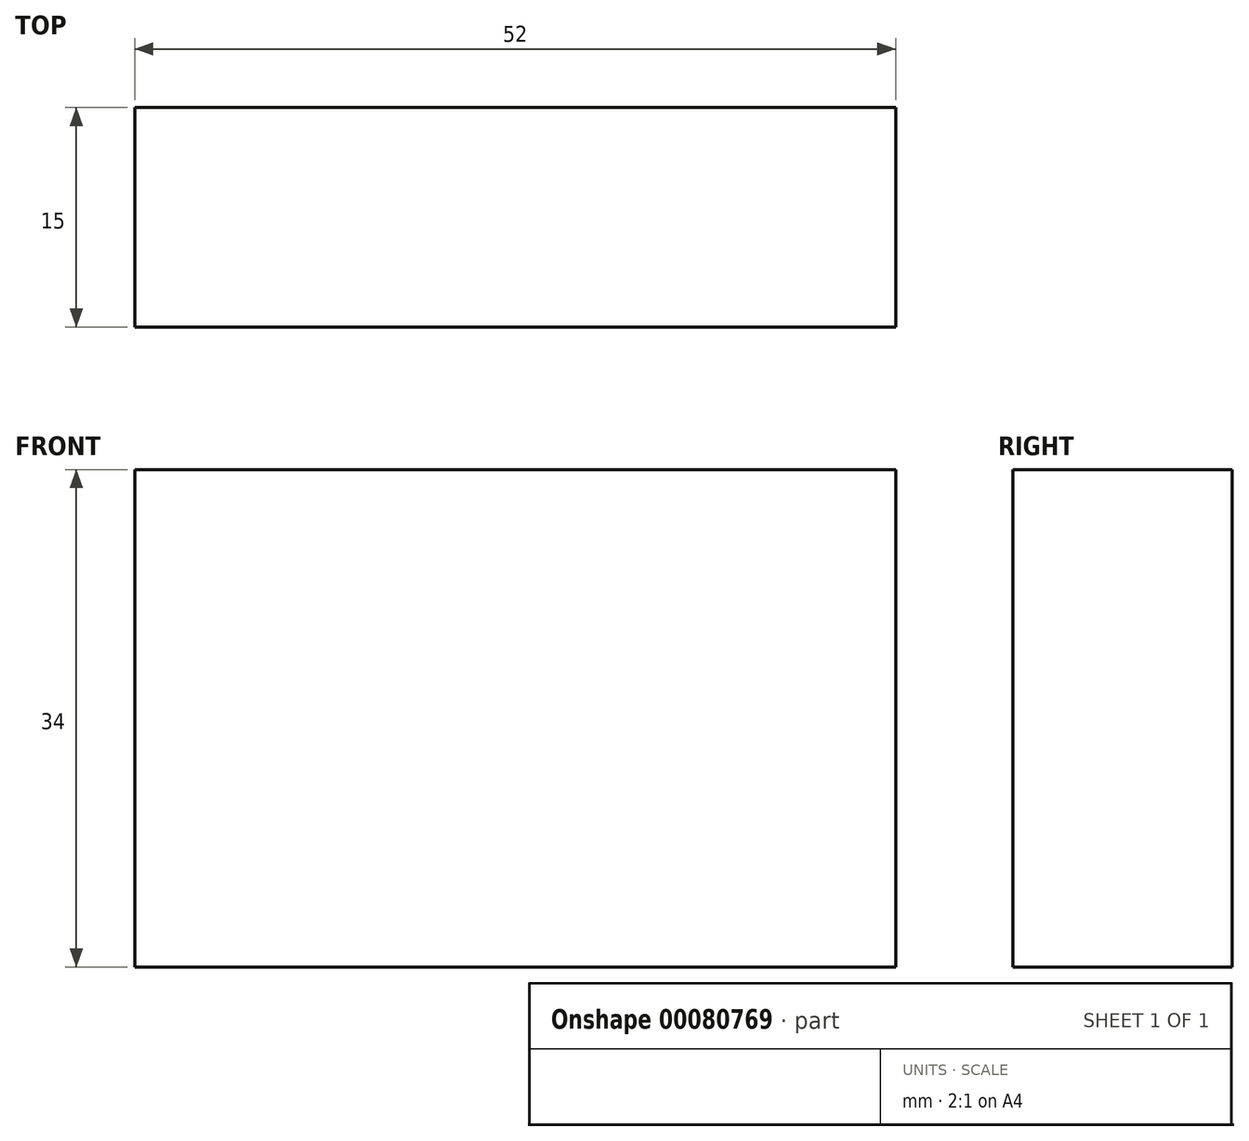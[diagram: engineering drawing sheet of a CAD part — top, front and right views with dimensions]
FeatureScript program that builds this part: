
annotation { "Feature Type Name" : "Feature", "Feature Type Description" : "" }
export const myFeature = defineFeature(function(context is Context, id is Id, definition is map)
    precondition{}
    {
        {
            var Q0;
            Q0=qCreatedBy(makeId("Front.planeOp"),FACE);
            var sketch = newSketch(context, id + "F0", { "sketchPlane" : qUnion([Q0])});
            skLineSegment(sketch, "E0.bottom", {"start": v(26, 17) * mm, "end": v(-26, 17) * mm});
            skLineSegment(sketch, "E0.top", {"start": v(26, -17) * mm, "end": v(-26, -17) * mm});
            skLineSegment(sketch, "E0.left", {"start": v(26, 17) * mm, "end": v(26, -17) * mm});
            skLineSegment(sketch, "E0.right", {"start": v(-26, 17) * mm, "end": v(-26, -17) * mm});
            skPoint(sketch, "E0.middle", {"position": v(0, 0) * mm});
            skSolve(sketch);
        }
        {
            var Q0;
            Q0=makeQuery(id+"F0.imprint","IMPRINT",FACE,{"disambiguationData":[TD([[makeQuery(id+"F0.imprint","IMPRINT",EDGE,{"derivedFrom":sQuery(id+"F0.wireOp",EDGE,"E0.bottom")}),1.0]])]});
            extrude(context, id + "F1", {"entities" : qUnion([Q0]), "depth" : 15 * mm});
        }
    });
